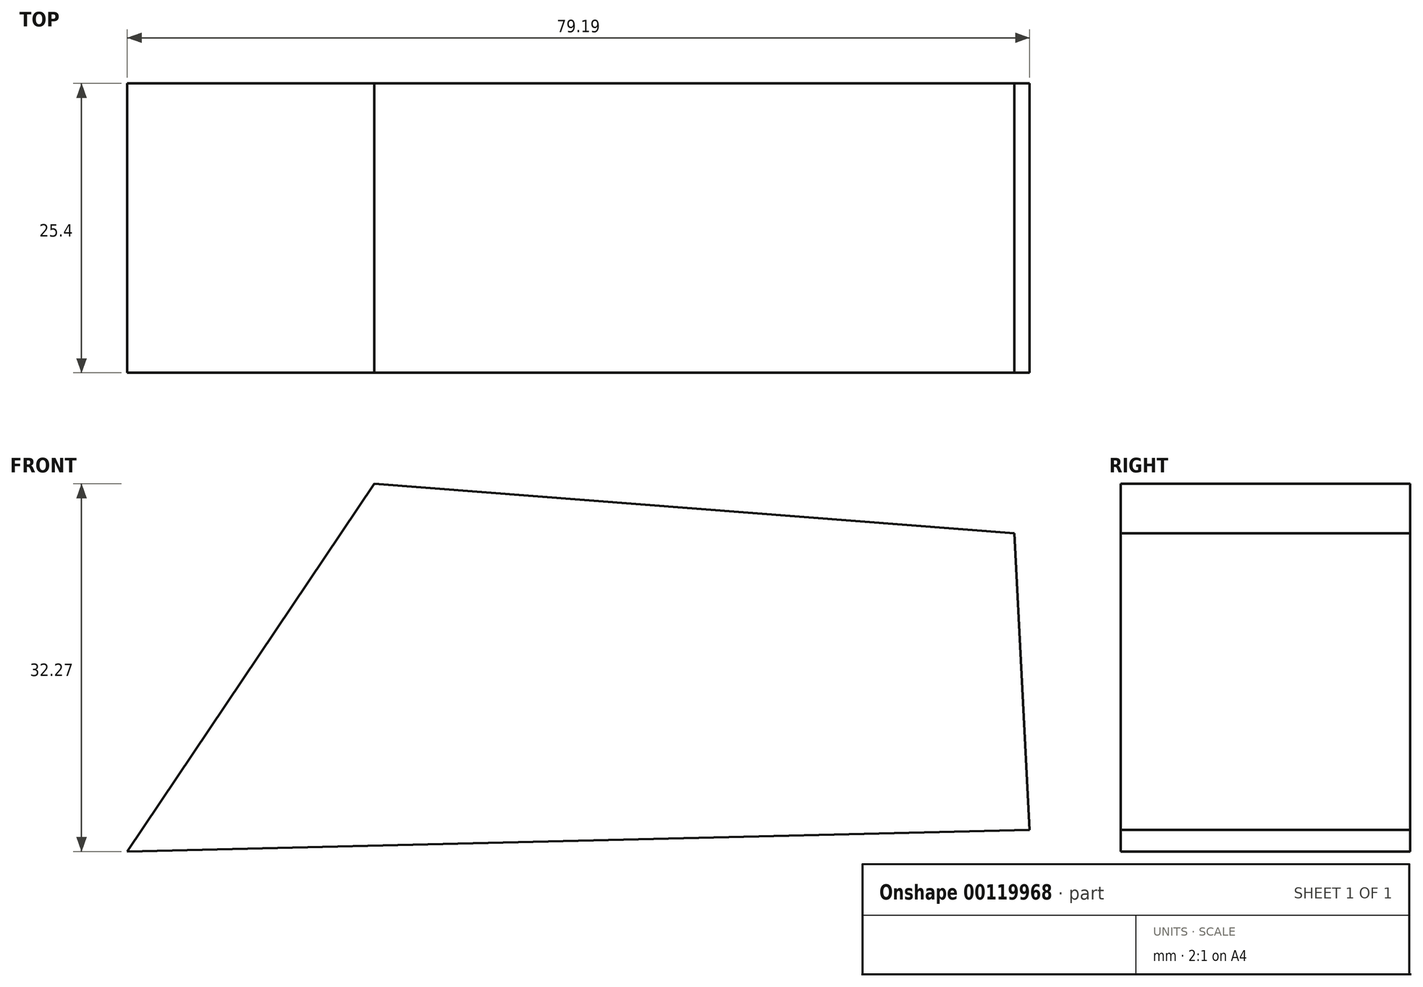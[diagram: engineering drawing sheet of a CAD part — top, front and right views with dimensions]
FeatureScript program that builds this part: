
annotation { "Feature Type Name" : "Feature", "Feature Type Description" : "" }
export const myFeature = defineFeature(function(context is Context, id is Id, definition is map)
    precondition{}
    {
        {
            var Q0;
            Q0=qCreatedBy(makeId("Front.planeOp"),FACE);
            var sketch = newSketch(context, id + "F0", { "sketchPlane" : qUnion([Q0])});
            skLineSegment(sketch, "E0", {"start": v(-34.72, 23.32) * mm, "end": v(21.43, 18.99) * mm});
            skLineSegment(sketch, "E1", {"start": v(21.43, 18.99) * mm, "end": v(22.78, -7.05) * mm});
            skLineSegment(sketch, "E2", {"start": v(22.78, -7.05) * mm, "end": v(-56.41, -8.95) * mm});
            skLineSegment(sketch, "E3", {"start": v(-56.41, -8.95) * mm, "end": v(-34.72, 23.32) * mm});
            skSolve(sketch);
        }
        {
            var Q0;
            Q0 = qSketchRegion(id + "F0", true);
            extrude(context, id + "F1", {"entities" : qUnion([Q0]), "depth" : 25.4 * mm});
        }
    });
